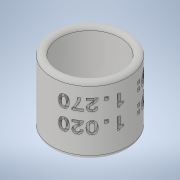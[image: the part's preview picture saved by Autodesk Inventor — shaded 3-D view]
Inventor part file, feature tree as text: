
AUTODESK INVENTOR PART (.ipt)
format: ipt  version: 2021.1 (Build 251245000, 245)  size: 573,952 bytes
history: native  units: in
note: dims shown in document units (in); Inventor stores cm internally (conversion verified against a paired STEP export)
features: sketch x3, extrude x2, fillet x2, plane x1, emboss x1
ambient origin geometry x8: Origin, YZ Plane, XZ Plane, XY Plane, X Axis, Y Axis, Z Axis, Center Point
bodies: Solid1 (feature_tree)
feature tree (9):
  extrude  "Extrusion1"  Depth=0.125in
  extrude  "Extrusion2"  Depth=1.27in
  plane  "Work Plane1"
  emboss  "Emboss1"
  fillet  "Fillet1"  Radius=1.02in
  fillet  "Fillet2"  Radius=1.0in
  sketch  "Sketch1"  dims[d0=1.27in d1=0.125in]
  sketch  "Sketch2"  dims[d2=0.0in d3=1.27in d4=1.02in d5=1.0in d6=0.0in]
  sketch  "Sketch3"  dims[d7=0.05in d8=0.0in d9=0.0625in d10=0.0625in]
